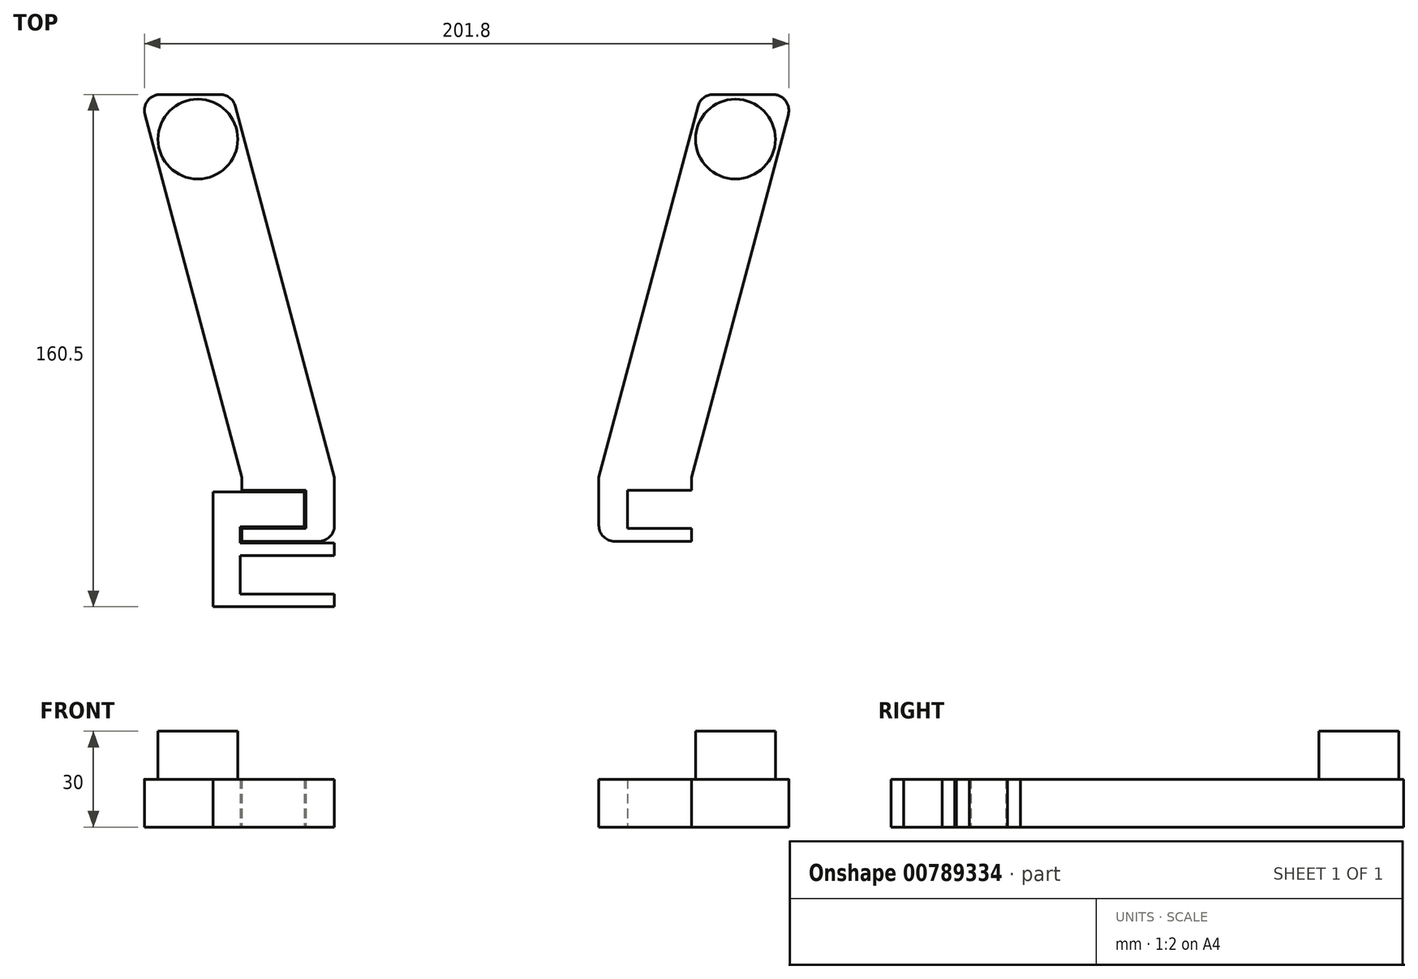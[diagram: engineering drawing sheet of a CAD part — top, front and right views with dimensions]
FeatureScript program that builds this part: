
annotation { "Feature Type Name" : "Feature", "Feature Type Description" : "" }
export const myFeature = defineFeature(function(context is Context, id is Id, definition is map)
    precondition{}
    {
        {
            var Q0;
            Q0=qCreatedBy(makeId("Top.planeOp"),FACE);
            var sketch = newSketch(context, id + "F0", { "sketchPlane" : qUnion([Q0])});
            skLineSegment(sketch, "E0", {"start": v(-70.4, -20) * mm, "end": v(-70.4, -16) * mm});
            skLineSegment(sketch, "E1", {"start": v(-70.4, -16) * mm, "end": v(-50.4, -16) * mm});
            skLineSegment(sketch, "E2", {"start": v(-50.4, -16) * mm, "end": v(-50.4, -4) * mm});
            skLineSegment(sketch, "E3", {"start": v(-50.4, -4) * mm, "end": v(-70.4, -4) * mm});
            skLineSegment(sketch, "E4", {"start": v(-70.4, -4) * mm, "end": v(-70.4, 0) * mm});
            skLineSegment(sketch, "E5", {"start": v(-70.4, -20) * mm, "end": v(-41.4, -20) * mm});
            skLineSegment(sketch, "E6", {"start": v(-41.4, -20) * mm, "end": v(-41.4, 0) * mm});
            skLineSegment(sketch, "E7", {"start": v(-41.4, 0) * mm, "end": v(-70.4, 0) * mm});
            skLineSegment(sketch, "E8", {"start": v(-41.4, 0) * mm, "end": v(-73.41, 120) * mm});
            skLineSegment(sketch, "E9", {"start": v(-102.41, 120) * mm, "end": v(-70.4, 0) * mm});
            skLineSegment(sketch, "E10", {"start": v(-102.41, 120) * mm, "end": v(-73.41, 120) * mm});
            skPoint(sketch, "E11", {"position": v(-87.91, 120) * mm});
            skPoint(sketch, "E12", {"position": v(-55.9, 0) * mm});
            skLineSegment(sketch, "E13", {"start": v(-87.91, 120) * mm, "end": v(-55.9, 0) * mm, "construction": true});
            skCircle(sketch, "E14", {"center": v(-84.17, 105.99) * mm, "radius": 12.5 * mm});
            skLineSegment(sketch, "E15.0", {"start": v(-50.9, -4.5) * mm, "end": v(-79.4, -4.5) * mm});
            skLineSegment(sketch, "E15.1", {"start": v(-50.9, -15.5) * mm, "end": v(-50.9, -4.5) * mm});
            skLineSegment(sketch, "E15.2", {"start": v(-79.4, -15.5) * mm, "end": v(-50.9, -15.5) * mm});
            skLineSegment(sketch, "E16", {"start": v(-79.4, -4.5) * mm, "end": v(-79.4, -15.5) * mm});
            skLineSegment(sketch, "E17", {"start": v(-70.9, -15.5) * mm, "end": v(-70.9, -24.5) * mm});
            skLineSegment(sketch, "E18", {"start": v(-70.9, -20.5) * mm, "end": v(-41.4, -20.5) * mm});
            skLineSegment(sketch, "E19", {"start": v(-70.9, -24.5) * mm, "end": v(-41.4, -24.5) * mm});
            skLineSegment(sketch, "E20", {"start": v(-41.4, -20.5) * mm, "end": v(-41.4, -24.5) * mm});
            skLineSegment(sketch, "E21", {"start": v(-79.4, -15.5) * mm, "end": v(-79.4, -40.5) * mm});
            skLineSegment(sketch, "E22", {"start": v(-79.4, -40.5) * mm, "end": v(-41.4, -40.5) * mm});
            skLineSegment(sketch, "E23", {"start": v(-41.4, -40.5) * mm, "end": v(-41.4, -36.5) * mm});
            skLineSegment(sketch, "E24", {"start": v(-41.4, -36.5) * mm, "end": v(-70.9, -36.5) * mm});
            skLineSegment(sketch, "E25", {"start": v(-70.9, -36.5) * mm, "end": v(-70.9, -24.5) * mm});
            skSolve(sketch);
        }
        {
            var Q0;
            Q0=makeQuery(id+"F0.imprint","IMPRINT",FACE,{"disambiguationData":[TD([[makeQuery(id+"F0.imprint","IMPRINT",EDGE,{"derivedFrom":sQuery(id+"F0.wireOp",EDGE,"E0")}),-1.0]])]});
            var Q1;
            Q1=makeQuery(id+"F0.imprint","IMPRINT",FACE,{"disambiguationData":[TD([[makeQuery(id+"F0.imprint","IMPRINT",EDGE,{"derivedFrom":sQuery(id+"F0.wireOp",EDGE,"E7")}),-1.0]])]});
            extrude(context, id + "F1", {"entities" : qUnion([Q0, Q1]), "depth" : 15 * mm, "offsetDistance" : 25 * mm});
        }
        {
            var Q0;
            Q0=makeQuery(id+"F0.imprint","IMPRINT",FACE,{"disambiguationData":[TD([[makeQuery(id+"F0.imprint","IMPRINT",EDGE,{"derivedFrom":sQuery(id+"F0.wireOp",EDGE,"x2kLiG3m-QAEO-T5TB-ed0j-9mi3EC8KzB30")}),1.0]])]});
            var Q1;
            Q1=makeQuery(id+"F0.imprint","IMPRINT",FACE,{"disambiguationData":[TD([[makeQuery(id+"F0.imprint","IMPRINT",EDGE,{"derivedFrom":sQuery(id+"F0.wireOp",EDGE,"E14")}),1.0]])]});
            extrude(context, id + "F2", {"entities" : qUnion([Q0, Q1]), "operationType" : NewBodyOperationType.ADD, "depth" : 30 * mm, "offsetDistance" : 25 * mm});
        }
        {
            var Q0;
            Q0=makeQuery(id+"F1.opExtrude","SWEPT_EDGE",EDGE,{"disambiguationData":[OSD([sQuery(id+"F0.wireOp",EDGE,"b3dAvVGk-qLFD-UKui-mPgT-5hXZM0cOb4ic"),sQuery(id+"F0.wireOp",EDGE,"E9")])]});
            var Q1;
            Q1=makeQuery(id+"F1.opExtrude","SWEPT_EDGE",EDGE,{"disambiguationData":[OSD([sQuery(id+"F0.wireOp",EDGE,"E8"),sQuery(id+"F0.wireOp",EDGE,"b3dAvVGk-qLFD-UKui-mPgT-5hXZM0cOb4ic")])]});
            var Q2;
            Q2=makeQuery(id+"F1.opExtrude","SWEPT_EDGE",EDGE,{"disambiguationData":[OSD([sQuery(id+"F0.wireOp",EDGE,"E5"),sQuery(id+"F0.wireOp",EDGE,"E6")])]});
            fillet(context, id + "F3", {"entities" : qUnion([Q0, Q1, Q2]), "radius" : 5 * mm, "tangentPropagation" : true, "allowEdgeOverflow" : false});
        }
        {
            var Q0;
            Q0=makeQuery(id+"F1.opExtrude","SWEPT_BODY",BODY,{"disambiguationData":[OSD([sQuery(id+"F0.wireOp",EDGE,"E0"),sQuery(id+"F0.wireOp",EDGE,"E1"),sQuery(id+"F0.wireOp",EDGE,"E2"),sQuery(id+"F0.wireOp",EDGE,"E3"),sQuery(id+"F0.wireOp",EDGE,"E4"),sQuery(id+"F0.wireOp",EDGE,"E5"),sQuery(id+"F0.wireOp",EDGE,"E6"),sQuery(id+"F0.wireOp",EDGE,"E8"),sQuery(id+"F0.wireOp",EDGE,"E9"),sQuery(id+"F0.wireOp",EDGE,"E10"),sQuery(id+"F0.wireOp",EDGE,"E14")])]});
            var Q1;
            Q1=qCreatedBy(makeId("Right.planeOp"),FACE);
            mirror(context, id + "F4", {"entities" : qUnion([Q0]), "mirrorPlane" : qUnion([Q1])});
        }
        {
            var Q0;
            {var subQ3=sQuery(id+"F0.wireOp",EDGE,"E21");Q0=makeQuery(id+"F0.imprint","IMPRINT",FACE,{"disambiguationData":[TD([[makeQuery(id+"F0.imprint","IMPRINT",EDGE,{"derivedFrom":subQ3}),1.0]])]});}
            var Q1;
            Q1=makeQuery(id+"F0.imprint","IMPRINT",FACE,{"disambiguationData":[TD([[makeQuery(id+"F0.imprint","IMPRINT",EDGE,{"derivedFrom":sQuery(id+"F0.wireOp",EDGE,"E15.0")}),1.0]])]});
            var Q2;
            {var subQ2=sQuery(id+"F0.wireOp",EDGE,"E18");Q2=makeQuery(id+"F0.imprint","IMPRINT",FACE,{"disambiguationData":[TD([[makeQuery(id+"F0.imprint","IMPRINT",EDGE,{"derivedFrom":subQ2}),-1.0]])]});}
            extrude(context, id + "F5", {"entities" : qUnion([Q0, Q1, Q2]), "depth" : 15 * mm, "offsetDistance" : 25 * mm});
        }
    });
